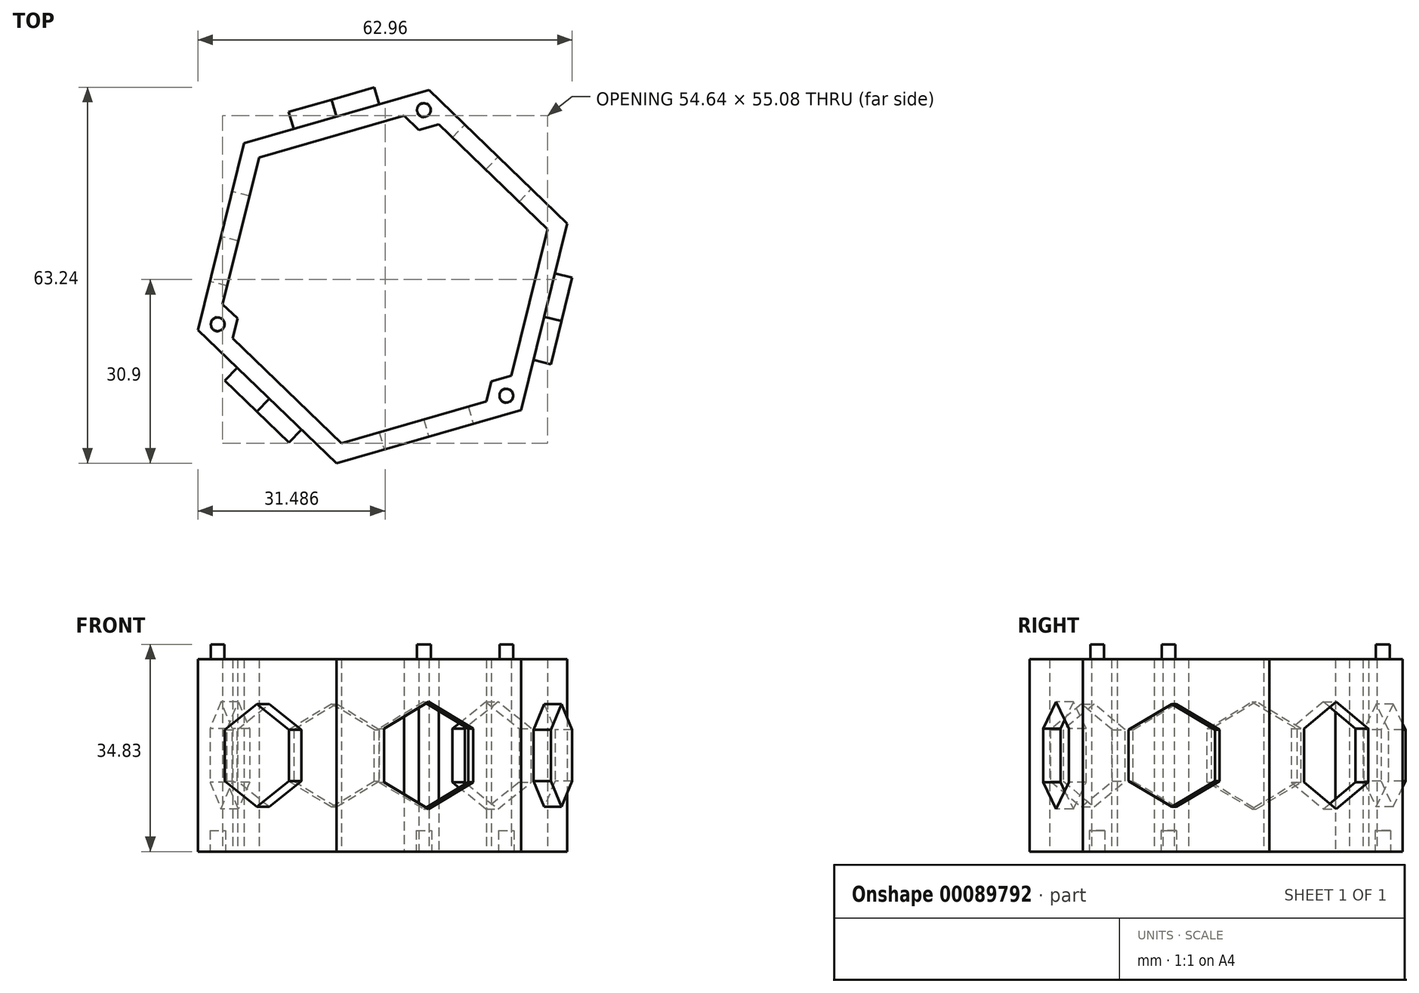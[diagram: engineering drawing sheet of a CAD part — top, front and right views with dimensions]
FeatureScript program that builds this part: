
annotation { "Feature Type Name" : "Feature", "Feature Type Description" : "" }
export const myFeature = defineFeature(function(context is Context, id is Id, definition is map)
    precondition{}
    {
        {
            var Q0;
            Q0=qCreatedBy(makeId("Top.planeOp"),FACE);
            var sketch = newSketch(context, id + "F0", { "sketchPlane" : qUnion([Q0])});
            skCircle(sketch, "E0.cCircle", {"center": v(0, 0) * mm, "radius": 32.33 * mm, "construction": true});
            skLineSegment(sketch, "E0.0", {"start": v(23.3, -22.42) * mm, "end": v(-7.77, -31.38) * mm});
            skLineSegment(sketch, "E0.1", {"start": v(-7.77, -31.38) * mm, "end": v(-31.07, -8.96) * mm});
            skLineSegment(sketch, "E0.2", {"start": v(-31.07, -8.96) * mm, "end": v(-23.3, 22.42) * mm});
            skLineSegment(sketch, "E0.3", {"start": v(-23.3, 22.42) * mm, "end": v(7.77, 31.38) * mm});
            skLineSegment(sketch, "E0.4", {"start": v(7.77, 31.38) * mm, "end": v(31.07, 8.96) * mm});
            skLineSegment(sketch, "E0.5", {"start": v(31.07, 8.96) * mm, "end": v(23.3, -22.42) * mm});
            skCircle(sketch, "E1.cCircle", {"center": v(0, 0) * mm, "radius": 28.87 * mm, "construction": true});
            skLineSegment(sketch, "E1.0", {"start": v(20.8, -20.02) * mm, "end": v(-6.94, -28.02) * mm});
            skLineSegment(sketch, "E1.1", {"start": v(-6.94, -28.02) * mm, "end": v(-27.74, -8) * mm});
            skLineSegment(sketch, "E1.2", {"start": v(-27.74, -8) * mm, "end": v(-20.8, 20.02) * mm});
            skLineSegment(sketch, "E1.3", {"start": v(-20.8, 20.02) * mm, "end": v(6.94, 28.02) * mm});
            skLineSegment(sketch, "E1.4", {"start": v(6.94, 28.02) * mm, "end": v(27.74, 8) * mm});
            skLineSegment(sketch, "E1.5", {"start": v(27.74, 8) * mm, "end": v(20.8, -20.02) * mm});
            skLineSegment(sketch, "E2.0", {"start": v(0, 0) * mm, "end": v(20.8, -20.02) * mm, "construction": true});
            skLineSegment(sketch, "E3", {"start": v(-26.9, -4.64) * mm, "end": v(-24.4, -7.04) * mm});
            skLineSegment(sketch, "E4", {"start": v(-24.4, -7.04) * mm, "end": v(-25.24, -10.4) * mm});
            skLineSegment(sketch, "E5", {"start": v(-31.07, -8.96) * mm, "end": v(-24.4, -7.04) * mm, "construction": true});
            skLineSegment(sketch, "E6", {"start": v(23.3, -22.42) * mm, "end": v(18.3, -17.62) * mm, "construction": true});
            skLineSegment(sketch, "E7", {"start": v(7.77, 31.38) * mm, "end": v(6.1, 24.66) * mm, "construction": true});
            skLineSegment(sketch, "E8", {"start": v(3.61, 27.06) * mm, "end": v(6.1, 24.66) * mm});
            skLineSegment(sketch, "E9", {"start": v(9.44, 25.62) * mm, "end": v(6.1, 24.66) * mm});
            skLineSegment(sketch, "E10", {"start": v(17.47, -20.98) * mm, "end": v(18.3, -17.62) * mm});
            skLineSegment(sketch, "E11", {"start": v(18.3, -17.62) * mm, "end": v(21.63, -16.66) * mm});
            skSolve(sketch);
        }
        {
            var Q0;
            {var subQ0=sQuery(id+"F0.wireOp",EDGE,"cb6c6618-7758-4560-adcc-7ff4b4ae14fa.0");Q0=makeQuery(id+"F0.imprint","IMPRINT",FACE,{"disambiguationData":[TD([[makeQuery(id+"F0.imprint","IMPRINT",EDGE,{"derivedFrom":subQ0}),-1.0]])]});}
            var Q1;
            {var subQ0=sQuery(id+"F0.wireOp",EDGE,"E0.0");Q1=makeQuery(id+"F0.imprint","IMPRINT",FACE,{"disambiguationData":[TD([[makeQuery(id+"F0.imprint","IMPRINT",EDGE,{"derivedFrom":subQ0}),-1.0]])]});}
            var Q2;
            Q2=makeQuery(id+"F0.imprint","IMPRINT",FACE,{"disambiguationData":[TD([[makeQuery(id+"F0.imprint","IMPRINT",EDGE,{"derivedFrom":sQuery(id+"F0.wireOp",EDGE,"f4d8d181-3e9a-4261-8a0c-2f3162c60284.0")}),-1.0]])]});
            var Q3;
            {var subQ4=sQuery(id+"F0.wireOp",EDGE,"E3");Q3=makeQuery(id+"F0.imprint","IMPRINT",FACE,{"disambiguationData":[TD([[makeQuery(id+"F0.imprint","IMPRINT",EDGE,{"derivedFrom":subQ4}),-1.0]])]});}
            var Q4;
            {var subQ3=sQuery(id+"F0.wireOp",EDGE,"E8");Q4=makeQuery(id+"F0.imprint","IMPRINT",FACE,{"disambiguationData":[TD([[makeQuery(id+"F0.imprint","IMPRINT",EDGE,{"derivedFrom":subQ3}),1.0]])]});}
            var Q5;
            {var subQ3=sQuery(id+"F0.wireOp",EDGE,"E10");Q5=makeQuery(id+"F0.imprint","IMPRINT",FACE,{"disambiguationData":[TD([[makeQuery(id+"F0.imprint","IMPRINT",EDGE,{"derivedFrom":subQ3}),-1.0]])]});}
            extrude(context, id + "F1", {"entities" : qUnion([Q0, Q1, Q2, Q3, Q4, Q5]), "depth" : 32.33 * mm});
        }
        {
            var Q0;
            Q0=makeQuery(id+"F1.opExtrude","CAP_FACE",FACE,{"disambiguationData":[OSD([sQuery(id+"F0.wireOp",EDGE,"cb6c6618-7758-4560-adcc-7ff4b4ae14fa.0"),sQuery(id+"F0.wireOp",EDGE,"cb6c6618-7758-4560-adcc-7ff4b4ae14fa.1"),sQuery(id+"F0.wireOp",EDGE,"cb6c6618-7758-4560-adcc-7ff4b4ae14fa.2"),sQuery(id+"F0.wireOp",EDGE,"cb6c6618-7758-4560-adcc-7ff4b4ae14fa.3"),sQuery(id+"F0.wireOp",EDGE,"cb6c6618-7758-4560-adcc-7ff4b4ae14fa.4"),sQuery(id+"F0.wireOp",EDGE,"cb6c6618-7758-4560-adcc-7ff4b4ae14fa.5"),sQuery(id+"F0.wireOp",EDGE,"ccf3cd0a-3b9a-433f-bdb1-acb9ccbccb68.0"),sQuery(id+"F0.wireOp",EDGE,"ccf3cd0a-3b9a-433f-bdb1-acb9ccbccb68.1"),sQuery(id+"F0.wireOp",EDGE,"ccf3cd0a-3b9a-433f-bdb1-acb9ccbccb68.2"),sQuery(id+"F0.wireOp",EDGE,"ccf3cd0a-3b9a-433f-bdb1-acb9ccbccb68.3"),sQuery(id+"F0.wireOp",EDGE,"ccf3cd0a-3b9a-433f-bdb1-acb9ccbccb68.4"),sQuery(id+"F0.wireOp",EDGE,"ccf3cd0a-3b9a-433f-bdb1-acb9ccbccb68.5"),sQuery(id+"F0.wireOp",EDGE,"E0.0"),sQuery(id+"F0.wireOp",EDGE,"E0.1"),sQuery(id+"F0.wireOp",EDGE,"E0.2"),sQuery(id+"F0.wireOp",EDGE,"E0.3"),sQuery(id+"F0.wireOp",EDGE,"E0.4"),sQuery(id+"F0.wireOp",EDGE,"E0.5"),sQuery(id+"F0.wireOp",EDGE,"E1.0"),sQuery(id+"F0.wireOp",EDGE,"E1.1"),sQuery(id+"F0.wireOp",EDGE,"E1.2"),sQuery(id+"F0.wireOp",EDGE,"E1.3"),sQuery(id+"F0.wireOp",EDGE,"E1.4"),sQuery(id+"F0.wireOp",EDGE,"E1.5"),sQuery(id+"F0.wireOp",EDGE,"f4d8d181-3e9a-4261-8a0c-2f3162c60284.0"),sQuery(id+"F0.wireOp",EDGE,"f4d8d181-3e9a-4261-8a0c-2f3162c60284.1"),sQuery(id+"F0.wireOp",EDGE,"f4d8d181-3e9a-4261-8a0c-2f3162c60284.2"),sQuery(id+"F0.wireOp",EDGE,"f4d8d181-3e9a-4261-8a0c-2f3162c60284.3"),sQuery(id+"F0.wireOp",EDGE,"f4d8d181-3e9a-4261-8a0c-2f3162c60284.4"),sQuery(id+"F0.wireOp",EDGE,"f4d8d181-3e9a-4261-8a0c-2f3162c60284.5"),sQuery(id+"F0.wireOp",EDGE,"d05c9255-d41b-4ef5-af4f-0391519c7850.0"),sQuery(id+"F0.wireOp",EDGE,"d05c9255-d41b-4ef5-af4f-0391519c7850.1"),sQuery(id+"F0.wireOp",EDGE,"d05c9255-d41b-4ef5-af4f-0391519c7850.2"),sQuery(id+"F0.wireOp",EDGE,"d05c9255-d41b-4ef5-af4f-0391519c7850.3"),sQuery(id+"F0.wireOp",EDGE,"d05c9255-d41b-4ef5-af4f-0391519c7850.4"),sQuery(id+"F0.wireOp",EDGE,"d05c9255-d41b-4ef5-af4f-0391519c7850.5")])],"isStart":true});
            var sketch = newSketch(context, id + "F2", { "sketchPlane" : qUnion([Q0])});
            skCircle(sketch, "E12", {"center": v(20.8, 20.02) * mm, "radius": 1.3 * mm});
            skCircle(sketch, "E13", {"center": v(6.94, -28.02) * mm, "radius": 1.3 * mm});
            skCircle(sketch, "E14", {"center": v(-27.74, 8) * mm, "radius": 1.3 * mm});
            skSolve(sketch);
        }
        {
            var Q0;
            Q0=qSketchRegion(id+"F2",true);
            extrude(context, id + "F3", {"entities" : qUnion([Q0]), "operationType" : NewBodyOperationType.REMOVE, "oppositeDirection" : true, "depth" : 3.5 * mm});
        }
        {
            var Q0;
            Q0=makeQuery(id+"F1.opExtrude","CAP_FACE",FACE,{"disambiguationData":[OSD([sQuery(id+"F0.wireOp",EDGE,"cb6c6618-7758-4560-adcc-7ff4b4ae14fa.0"),sQuery(id+"F0.wireOp",EDGE,"cb6c6618-7758-4560-adcc-7ff4b4ae14fa.1"),sQuery(id+"F0.wireOp",EDGE,"cb6c6618-7758-4560-adcc-7ff4b4ae14fa.2"),sQuery(id+"F0.wireOp",EDGE,"cb6c6618-7758-4560-adcc-7ff4b4ae14fa.3"),sQuery(id+"F0.wireOp",EDGE,"cb6c6618-7758-4560-adcc-7ff4b4ae14fa.4"),sQuery(id+"F0.wireOp",EDGE,"cb6c6618-7758-4560-adcc-7ff4b4ae14fa.5"),sQuery(id+"F0.wireOp",EDGE,"ccf3cd0a-3b9a-433f-bdb1-acb9ccbccb68.0"),sQuery(id+"F0.wireOp",EDGE,"ccf3cd0a-3b9a-433f-bdb1-acb9ccbccb68.1"),sQuery(id+"F0.wireOp",EDGE,"ccf3cd0a-3b9a-433f-bdb1-acb9ccbccb68.2"),sQuery(id+"F0.wireOp",EDGE,"ccf3cd0a-3b9a-433f-bdb1-acb9ccbccb68.3"),sQuery(id+"F0.wireOp",EDGE,"ccf3cd0a-3b9a-433f-bdb1-acb9ccbccb68.4"),sQuery(id+"F0.wireOp",EDGE,"ccf3cd0a-3b9a-433f-bdb1-acb9ccbccb68.5"),sQuery(id+"F0.wireOp",EDGE,"E0.0"),sQuery(id+"F0.wireOp",EDGE,"E0.1"),sQuery(id+"F0.wireOp",EDGE,"E0.2"),sQuery(id+"F0.wireOp",EDGE,"E0.3"),sQuery(id+"F0.wireOp",EDGE,"E0.4"),sQuery(id+"F0.wireOp",EDGE,"E0.5"),sQuery(id+"F0.wireOp",EDGE,"E1.0"),sQuery(id+"F0.wireOp",EDGE,"E1.1"),sQuery(id+"F0.wireOp",EDGE,"E1.2"),sQuery(id+"F0.wireOp",EDGE,"E1.3"),sQuery(id+"F0.wireOp",EDGE,"E1.4"),sQuery(id+"F0.wireOp",EDGE,"E1.5"),sQuery(id+"F0.wireOp",EDGE,"f4d8d181-3e9a-4261-8a0c-2f3162c60284.0"),sQuery(id+"F0.wireOp",EDGE,"f4d8d181-3e9a-4261-8a0c-2f3162c60284.1"),sQuery(id+"F0.wireOp",EDGE,"f4d8d181-3e9a-4261-8a0c-2f3162c60284.2"),sQuery(id+"F0.wireOp",EDGE,"f4d8d181-3e9a-4261-8a0c-2f3162c60284.3"),sQuery(id+"F0.wireOp",EDGE,"f4d8d181-3e9a-4261-8a0c-2f3162c60284.4"),sQuery(id+"F0.wireOp",EDGE,"f4d8d181-3e9a-4261-8a0c-2f3162c60284.5"),sQuery(id+"F0.wireOp",EDGE,"d05c9255-d41b-4ef5-af4f-0391519c7850.0"),sQuery(id+"F0.wireOp",EDGE,"d05c9255-d41b-4ef5-af4f-0391519c7850.1"),sQuery(id+"F0.wireOp",EDGE,"d05c9255-d41b-4ef5-af4f-0391519c7850.2"),sQuery(id+"F0.wireOp",EDGE,"d05c9255-d41b-4ef5-af4f-0391519c7850.3"),sQuery(id+"F0.wireOp",EDGE,"d05c9255-d41b-4ef5-af4f-0391519c7850.4"),sQuery(id+"F0.wireOp",EDGE,"d05c9255-d41b-4ef5-af4f-0391519c7850.5")])],"isStart":false});
            var sketch = newSketch(context, id + "F4", { "sketchPlane" : qUnion([Q0])});
            skCircle(sketch, "E15", {"center": v(6.94, 28.02) * mm, "radius": 1.15 * mm});
            skCircle(sketch, "E16", {"center": v(20.8, -20.02) * mm, "radius": 1.15 * mm});
            skCircle(sketch, "E17", {"center": v(-27.74, -8) * mm, "radius": 1.15 * mm});
            skLineSegment(sketch, "E18", {"start": v(-31.07, -8.96) * mm, "end": v(31.07, 8.96) * mm, "construction": true});
            skLineSegment(sketch, "E19", {"start": v(-6.94, -28.02) * mm, "end": v(7.77, 31.38) * mm, "construction": true});
            skLineSegment(sketch, "E20", {"start": v(-23.3, 22.42) * mm, "end": v(23.3, -22.42) * mm, "construction": true});
            skSolve(sketch);
        }
        {
            var Q0;
            Q0=qSketchRegion(id+"F4",true);
            extrude(context, id + "F5", {"entities" : qUnion([Q0]), "operationType" : NewBodyOperationType.ADD, "depth" : 2.5 * mm});
        }
        {
            var Q0;
            Q0=makeQuery(id+"F1.opExtrude","SWEPT_FACE",FACE,{"disambiguationData":[OSD([sQuery(id+"F0.wireOp",EDGE,"E0.2")])]});
            var sketch = newSketch(context, id + "F6", { "sketchPlane" : qUnion([Q0])});
            skCircle(sketch, "E21.cCircle", {"center": v(0, 16.17) * mm, "radius": 7.8 * mm, "construction": true});
            skLineSegment(sketch, "E21.0", {"start": v(-7.8, 11.66) * mm, "end": v(-7.8, 20.67) * mm});
            skLineSegment(sketch, "E21.1", {"start": v(-7.8, 20.67) * mm, "end": v(0, 25.17) * mm});
            skLineSegment(sketch, "E21.2", {"start": v(0, 25.17) * mm, "end": v(7.8, 20.67) * mm});
            skLineSegment(sketch, "E21.3", {"start": v(7.8, 20.67) * mm, "end": v(7.8, 11.66) * mm});
            skLineSegment(sketch, "E21.4", {"start": v(7.8, 11.66) * mm, "end": v(0, 7.16) * mm});
            skLineSegment(sketch, "E21.5", {"start": v(0, 7.16) * mm, "end": v(-7.8, 11.66) * mm});
            skPoint(sketch, "E21.0.midPoint", {"position": v(-7.8, 16.17) * mm});
            skLineSegment(sketch, "E22", {"start": v(42.99, 16.17) * mm, "end": v(-42.99, 16.17) * mm, "construction": true});
            skPoint(sketch, "E23", {"position": v(-16.17, 16.17) * mm});
            skSolve(sketch);
        }
        {
            var Q0;
            Q0=makeQuery(id+"F1.opExtrude","SWEPT_FACE",FACE,{"disambiguationData":[OSD([sQuery(id+"F0.wireOp",EDGE,"E0.3")])]});
            var sketch = newSketch(context, id + "F7", { "sketchPlane" : qUnion([Q0])});
            skCircle(sketch, "E24.cCircle", {"center": v(0, 16.17) * mm, "radius": 7.5 * mm, "construction": true});
            skLineSegment(sketch, "E24.0", {"start": v(-7.5, 11.84) * mm, "end": v(-7.5, 20.5) * mm});
            skLineSegment(sketch, "E24.1", {"start": v(-7.5, 20.5) * mm, "end": v(0, 24.83) * mm});
            skLineSegment(sketch, "E24.2", {"start": v(0, 24.83) * mm, "end": v(7.5, 20.5) * mm});
            skLineSegment(sketch, "E24.3", {"start": v(7.5, 20.5) * mm, "end": v(7.5, 11.84) * mm});
            skLineSegment(sketch, "E24.4", {"start": v(7.5, 11.84) * mm, "end": v(0, 7.5) * mm});
            skLineSegment(sketch, "E24.5", {"start": v(0, 7.5) * mm, "end": v(-7.5, 11.84) * mm});
            skPoint(sketch, "E24.0.midPoint", {"position": v(-7.5, 16.17) * mm});
            skLineSegment(sketch, "E25", {"start": v(0, 0) * mm, "end": v(0, 32.33) * mm, "construction": true});
            skSolve(sketch);
        }
        {
            var Q0;
            Q0=makeQuery(id+"F1.opExtrude","SWEPT_FACE",FACE,{"disambiguationData":[OSD([sQuery(id+"F0.wireOp",EDGE,"E0.4")])]});
            var sketch = newSketch(context, id + "F8", { "sketchPlane" : qUnion([Q0])});
            skCircle(sketch, "E26.cCircle", {"center": v(0, 16.17) * mm, "radius": 7.8 * mm, "construction": true});
            skLineSegment(sketch, "E26.0", {"start": v(-7.8, 11.66) * mm, "end": v(-7.8, 20.67) * mm});
            skLineSegment(sketch, "E26.1", {"start": v(-7.8, 20.67) * mm, "end": v(0, 25.17) * mm});
            skLineSegment(sketch, "E26.2", {"start": v(0, 25.17) * mm, "end": v(7.8, 20.67) * mm});
            skLineSegment(sketch, "E26.3", {"start": v(7.8, 20.67) * mm, "end": v(7.8, 11.66) * mm});
            skLineSegment(sketch, "E26.4", {"start": v(7.8, 11.66) * mm, "end": v(0, 7.16) * mm});
            skLineSegment(sketch, "E26.5", {"start": v(0, 7.16) * mm, "end": v(-7.8, 11.66) * mm});
            skPoint(sketch, "E26.0.midPoint", {"position": v(-7.8, 16.17) * mm});
            skLineSegment(sketch, "E27", {"start": v(0, 32.33) * mm, "end": v(0, 0) * mm, "construction": true});
            skSolve(sketch);
        }
        {
            var Q0;
            Q0=makeQuery(id+"F1.opExtrude","SWEPT_FACE",FACE,{"disambiguationData":[OSD([sQuery(id+"F0.wireOp",EDGE,"E0.5")])]});
            var sketch = newSketch(context, id + "F9", { "sketchPlane" : qUnion([Q0])});
            skCircle(sketch, "E28.cCircle", {"center": v(0, 16.17) * mm, "radius": 7.5 * mm, "construction": true});
            skLineSegment(sketch, "E28.0", {"start": v(-7.5, 11.84) * mm, "end": v(-7.5, 20.5) * mm});
            skLineSegment(sketch, "E28.1", {"start": v(-7.5, 20.5) * mm, "end": v(0, 24.83) * mm});
            skLineSegment(sketch, "E28.2", {"start": v(0, 24.83) * mm, "end": v(7.5, 20.5) * mm});
            skLineSegment(sketch, "E28.3", {"start": v(7.5, 20.5) * mm, "end": v(7.5, 11.84) * mm});
            skLineSegment(sketch, "E28.4", {"start": v(7.5, 11.84) * mm, "end": v(0, 7.5) * mm});
            skLineSegment(sketch, "E28.5", {"start": v(0, 7.5) * mm, "end": v(-7.5, 11.84) * mm});
            skPoint(sketch, "E28.0.midPoint", {"position": v(-7.5, 16.17) * mm});
            skLineSegment(sketch, "E29", {"start": v(0, 32.33) * mm, "end": v(0, 0) * mm, "construction": true});
            skSolve(sketch);
        }
        {
            var Q0;
            Q0=makeQuery(id+"F1.opExtrude","SWEPT_FACE",FACE,{"disambiguationData":[OSD([sQuery(id+"F0.wireOp",EDGE,"E0.0")])]});
            var sketch = newSketch(context, id + "F10", { "sketchPlane" : qUnion([Q0])});
            skCircle(sketch, "E30.cCircle", {"center": v(0, 16.17) * mm, "radius": 7.8 * mm, "construction": true});
            skLineSegment(sketch, "E30.0", {"start": v(-7.8, 11.66) * mm, "end": v(-7.8, 20.67) * mm});
            skLineSegment(sketch, "E30.1", {"start": v(-7.8, 20.67) * mm, "end": v(0, 25.17) * mm});
            skLineSegment(sketch, "E30.2", {"start": v(0, 25.17) * mm, "end": v(7.8, 20.67) * mm});
            skLineSegment(sketch, "E30.3", {"start": v(7.8, 20.67) * mm, "end": v(7.8, 11.66) * mm});
            skLineSegment(sketch, "E30.4", {"start": v(7.8, 11.66) * mm, "end": v(0, 7.16) * mm});
            skLineSegment(sketch, "E30.5", {"start": v(0, 7.16) * mm, "end": v(-7.8, 11.66) * mm});
            skPoint(sketch, "E30.0.midPoint", {"position": v(-7.8, 16.17) * mm});
            skLineSegment(sketch, "E31", {"start": v(0, 32.33) * mm, "end": v(0, 0) * mm, "construction": true});
            skSolve(sketch);
        }
        {
            var Q0;
            Q0=makeQuery(id+"F1.opExtrude","SWEPT_FACE",FACE,{"disambiguationData":[OSD([sQuery(id+"F0.wireOp",EDGE,"E0.1")])]});
            var sketch = newSketch(context, id + "F11", { "sketchPlane" : qUnion([Q0])});
            skCircle(sketch, "E32.cCircle", {"center": v(0.49, 16.17) * mm, "radius": 7.5 * mm, "construction": true});
            skLineSegment(sketch, "E32.0", {"start": v(-7.01, 11.84) * mm, "end": v(-7.01, 20.5) * mm});
            skLineSegment(sketch, "E32.1", {"start": v(-7.01, 20.5) * mm, "end": v(0.49, 24.83) * mm});
            skLineSegment(sketch, "E32.2", {"start": v(0.49, 24.83) * mm, "end": v(7.99, 20.5) * mm});
            skLineSegment(sketch, "E32.3", {"start": v(7.99, 20.5) * mm, "end": v(7.99, 11.84) * mm});
            skLineSegment(sketch, "E32.4", {"start": v(7.99, 11.84) * mm, "end": v(0.49, 7.5) * mm});
            skLineSegment(sketch, "E32.5", {"start": v(0.49, 7.5) * mm, "end": v(-7.01, 11.84) * mm});
            skPoint(sketch, "E32.0.midPoint", {"position": v(-7.01, 16.17) * mm});
            skLineSegment(sketch, "E33", {"start": v(0.98, 32.33) * mm, "end": v(0, 0) * mm, "construction": true});
            skSolve(sketch);
        }
        {
            var Q0;
            Q0 = qSketchRegion(id + "F9", true);
            extrude(context, id + "F12", {"entities" : qUnion([Q0]), "operationType" : NewBodyOperationType.ADD, "depth" : 3 * mm});
        }
        {
            var Q0;
            Q0 = qSketchRegion(id + "F7", true);
            extrude(context, id + "F13", {"entities" : qUnion([Q0]), "operationType" : NewBodyOperationType.ADD, "depth" : 3 * mm});
        }
        {
            var Q0;
            Q0 = qSketchRegion(id + "F11", true);
            extrude(context, id + "F14", {"entities" : qUnion([Q0]), "operationType" : NewBodyOperationType.ADD, "depth" : 3 * mm});
        }
        {
            var Q0;
            Q0 = qSketchRegion(id + "F10", true);
            extrude(context, id + "F15", {"entities" : qUnion([Q0]), "operationType" : NewBodyOperationType.REMOVE, "endBound" : BoundingType.UP_TO_NEXT, "oppositeDirection" : true, "depth" : 25 * mm});
        }
        {
            var Q0;
            Q0 = qSketchRegion(id + "F6", true);
            extrude(context, id + "F16", {"entities" : qUnion([Q0]), "operationType" : NewBodyOperationType.REMOVE, "endBound" : BoundingType.UP_TO_NEXT, "oppositeDirection" : true, "depth" : 25 * mm});
        }
        {
            var Q0;
            Q0 = qSketchRegion(id + "F8", true);
            extrude(context, id + "F17", {"entities" : qUnion([Q0]), "operationType" : NewBodyOperationType.REMOVE, "endBound" : BoundingType.UP_TO_NEXT, "oppositeDirection" : true, "depth" : 25 * mm});
        }
    });
